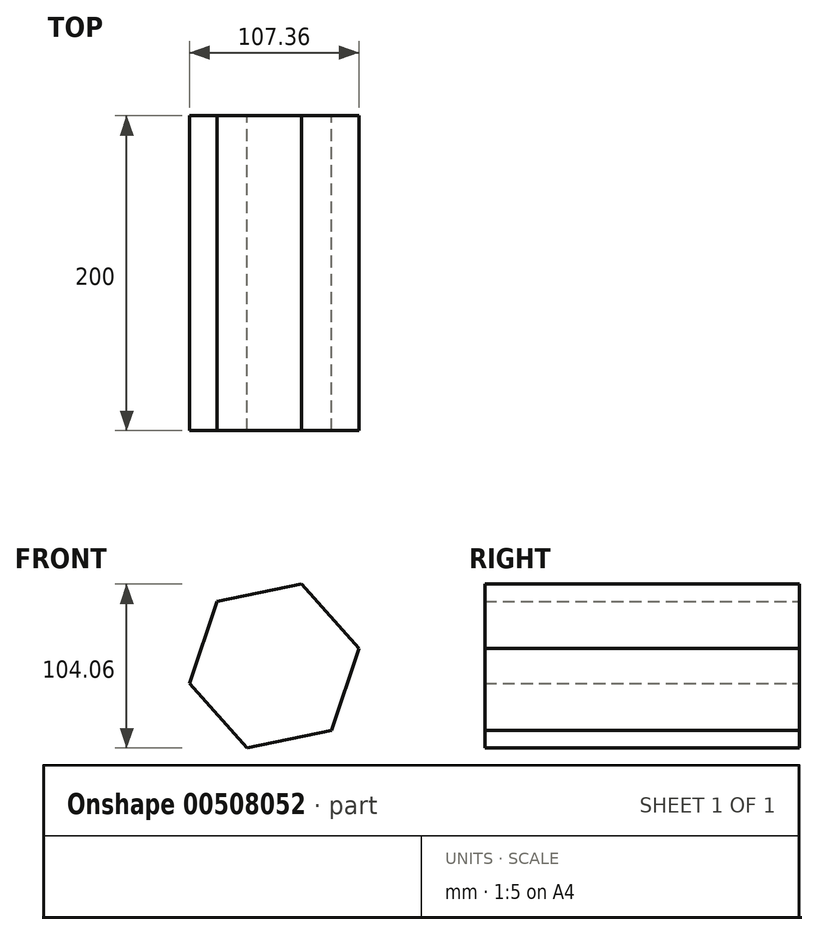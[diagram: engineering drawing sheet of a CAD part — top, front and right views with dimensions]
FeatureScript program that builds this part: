
annotation { "Feature Type Name" : "Feature", "Feature Type Description" : "" }
export const myFeature = defineFeature(function(context is Context, id is Id, definition is map)
    precondition{}
    {
        {
            var Q0;
            Q0=qCreatedBy(makeId("Front.planeOp"),FACE);
            var sketch = newSketch(context, id + "F0", { "sketchPlane" : qUnion([Q0])});
            skCircle(sketch, "E0.cCircle", {"center": v(0, 0) * mm, "radius": 54.81 * mm, "construction": true});
            skLineSegment(sketch, "E0.0", {"start": v(-36.43, 40.95) * mm, "end": v(17.25, 52.03) * mm});
            skLineSegment(sketch, "E0.1", {"start": v(17.25, 52.03) * mm, "end": v(53.68, 11.08) * mm});
            skLineSegment(sketch, "E0.2", {"start": v(53.68, 11.08) * mm, "end": v(36.43, -40.95) * mm});
            skLineSegment(sketch, "E0.3", {"start": v(36.43, -40.95) * mm, "end": v(-17.25, -52.03) * mm});
            skLineSegment(sketch, "E0.4", {"start": v(-17.25, -52.03) * mm, "end": v(-53.68, -11.08) * mm});
            skLineSegment(sketch, "E0.5", {"start": v(-53.68, -11.08) * mm, "end": v(-36.43, 40.95) * mm});
            skSolve(sketch);
        }
        {
            var Q0;
            Q0=makeQuery(id+"F0.imprint","IMPRINT",FACE,{"disambiguationData":[TD([[makeQuery(id+"F0.imprint","IMPRINT",EDGE,{"derivedFrom":sQuery(id+"F0.wireOp",EDGE,"E0.0")}),-1.0]])]});
            extrude(context, id + "F1", {"entities" : qUnion([Q0]), "endBound" : BoundingType.SYMMETRIC, "depth" : 200 * mm});
        }
    });
